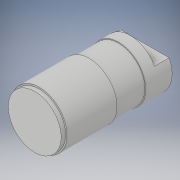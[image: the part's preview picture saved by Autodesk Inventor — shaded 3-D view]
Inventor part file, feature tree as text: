
AUTODESK INVENTOR PART (.ipt)
format: ipt  version: 2017 (Build 210142000, 142)  size: 674,816 bytes
history: native  units: in
note: dims shown in document units (in); Inventor stores cm internally (conversion verified against a paired STEP export)
features: extrude x1, sketch x1, other x1
ambient origin geometry x8: Origin, YZ Plane, XZ Plane, XY Plane, X Axis, Y Axis, Z Axis, Center Point
bodies: Solid1 (feature_tree)
feature tree (3):
  extrude  "Extrusion1"  [1 undecoded]
  sketch  "Sketch1"  dims[d0=2.3041in d1=0.0in]
  other  "Boss-Extrude10"
note: 1 required parameter value undecoded (feature->parameter linkage not recoverable at this tier; creation-order binding heuristic only, values carry confidence <= 0.55)
